# Revit family: FMK11_63_UN_Surface-mounted_ETK
name_source: partatom
category: Lighting Fixtures
revit_build: Autodesk Revit 2017 (Build: 20190508_0315(x64)
units: mm (PartAtom-declared; Revit-internal decimal feet)

## family parameters
Always vertical = Yes
Cut with Voids When Loaded = No
Light Source = No
OmniClass Number = 23.80.70.11.14.11
OmniClass Title = Downlights
Part Type = Normal
Room Calculation Point = Yes
Round Connector Dimension = Use Diameter
Shared = No
Work Plane-Based = No

## types (6) — shared parameters
40mm Height = No
48mm Height = Yes
Apparent Load = 12 VA
Assembly Code = 63.0
Bundle = 120°
Calc_Radius = 117 mm
Description = Surface Mounted
Diameter = 250 mm
IfcExportAs = IfcLightFixtureType
IfcExportType = USERDEFINED
Lamp = LED
Luminaire_Body_Material = PPS Plastic
Manufacturer = ETK licht B.V.
Model = FMK.1
Radius = 125 mm
Type Comments = IP54 - IK08
URL = https://www.etk.nl
Voltage = 230 V
Wattage Comments = 12W

## type names (no varying parameters)
- FMK.1109.10 - Ø250x48 / 12W
- FMK.1129.10 - Ø250x48 / 12W
- FMK.1139.10 - Ø250x48 / 12W
- FMK.1109.10N - Ø250x48 / 12W
- FMK.1129.10N - Ø250x48 / 12W
- FMK.1139.10N - Ø250x48 / 12W

## geometry (parser evidence)
native form markers: Sweep x6
no freeform markers — native parametric forms only
